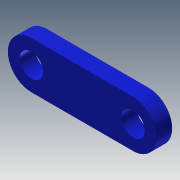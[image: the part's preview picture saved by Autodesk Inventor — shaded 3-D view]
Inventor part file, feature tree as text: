
AUTODESK INVENTOR PART (.ipt)
format: ipt  version: 2013 (Build 170138000, 138)  size: 94,720 bytes
history: native  units: mm
features: extrude x2, sketch x2
ambient origin geometry x8: Origin, YZ Plane, XZ Plane, XY Plane, X Axis, Y Axis, Z Axis, Center Point
bodies: Solid1 (feature_tree)
feature tree (4):
  extrude  "Extrusion1"  Depth=6.0mm
  extrude  "Extrusion2"  Depth=6.0mm
  sketch  "Sketch1"  dims[d0=13.0mm d1=6.0mm]
  sketch  "Sketch2"  dims[d2=6.0mm d3=6.0mm d4=2.0mm d5=0.0mm d6=3.0mm d7=3.0mm d8=2.0mm d9=0.0mm]
